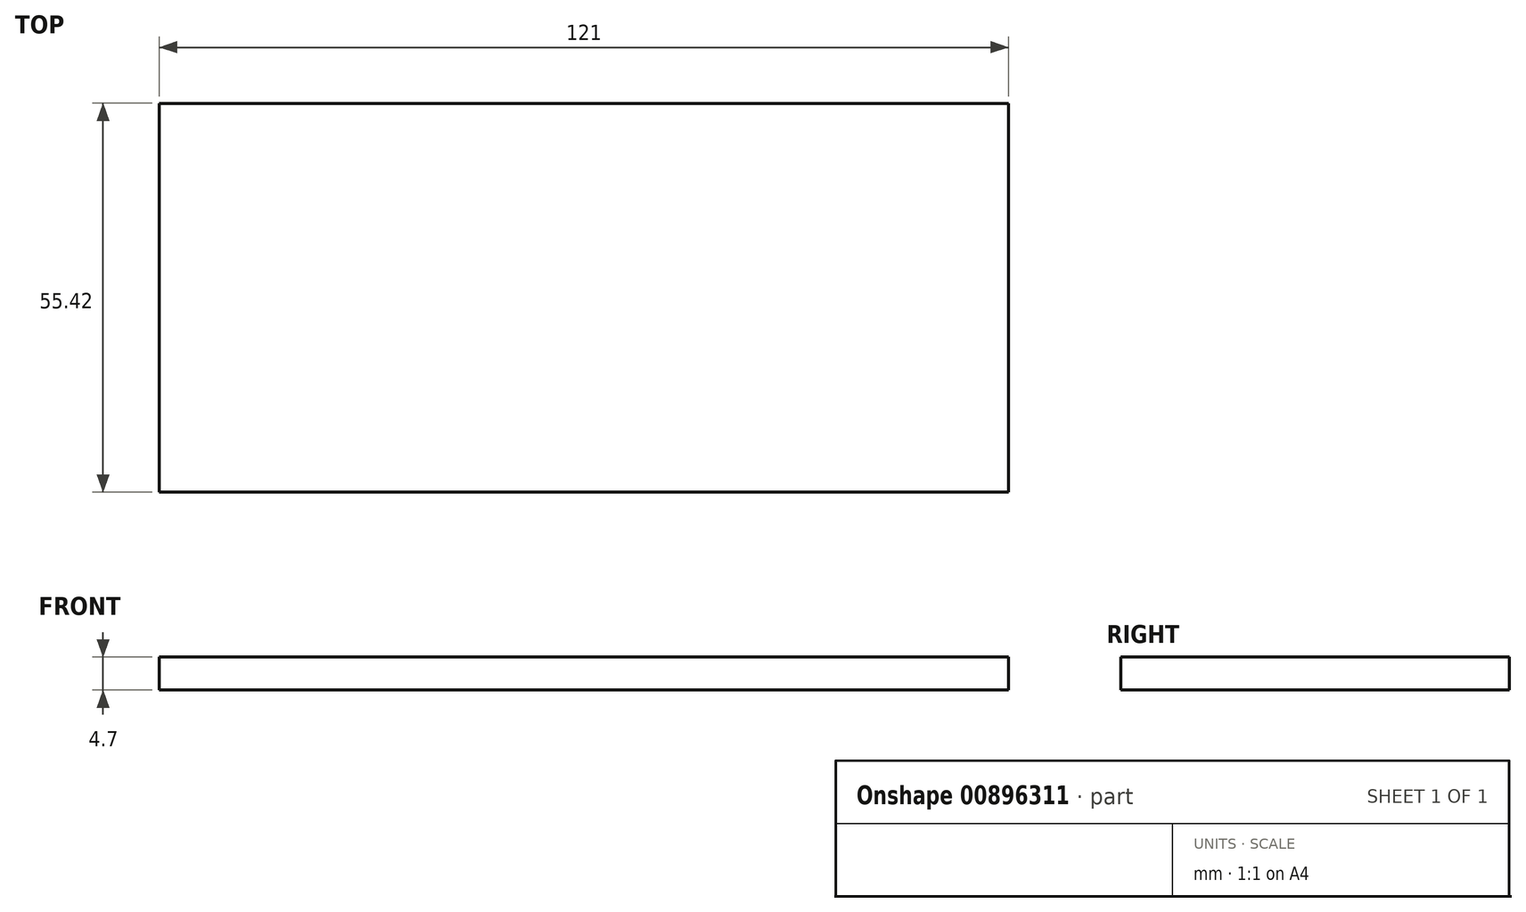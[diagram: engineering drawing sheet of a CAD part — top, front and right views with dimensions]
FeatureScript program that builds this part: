
annotation { "Feature Type Name" : "Feature", "Feature Type Description" : "" }
export const myFeature = defineFeature(function(context is Context, id is Id, definition is map)
    precondition{}
    {
        {
            var Q0;
            Q0=qCreatedBy(makeId("Top.planeOp"),FACE);
            var sketch = newSketch(context, id + "F0", { "sketchPlane" : qUnion([Q0])});
            skLineSegment(sketch, "E0.bottom", {"start": v(-60.5, 27.7) * mm, "end": v(60.5, 27.7) * mm});
            skLineSegment(sketch, "E0.top", {"start": v(-60.5, -27.7) * mm, "end": v(60.5, -27.7) * mm});
            skLineSegment(sketch, "E0.left", {"start": v(-60.5, 27.7) * mm, "end": v(-60.5, -27.7) * mm});
            skLineSegment(sketch, "E0.right", {"start": v(60.5, 27.7) * mm, "end": v(60.5, -27.7) * mm});
            skPoint(sketch, "E0.middle", {"position": v(0, 0) * mm});
            skSolve(sketch);
        }
        {
            var Q0;
            Q0 = qSketchRegion(id + "F0", true);
            extrude(context, id + "F1", {"entities" : qUnion([Q0]), "depth" : 4.7 * mm, "offsetDistance" : 25 * mm});
        }
    });
